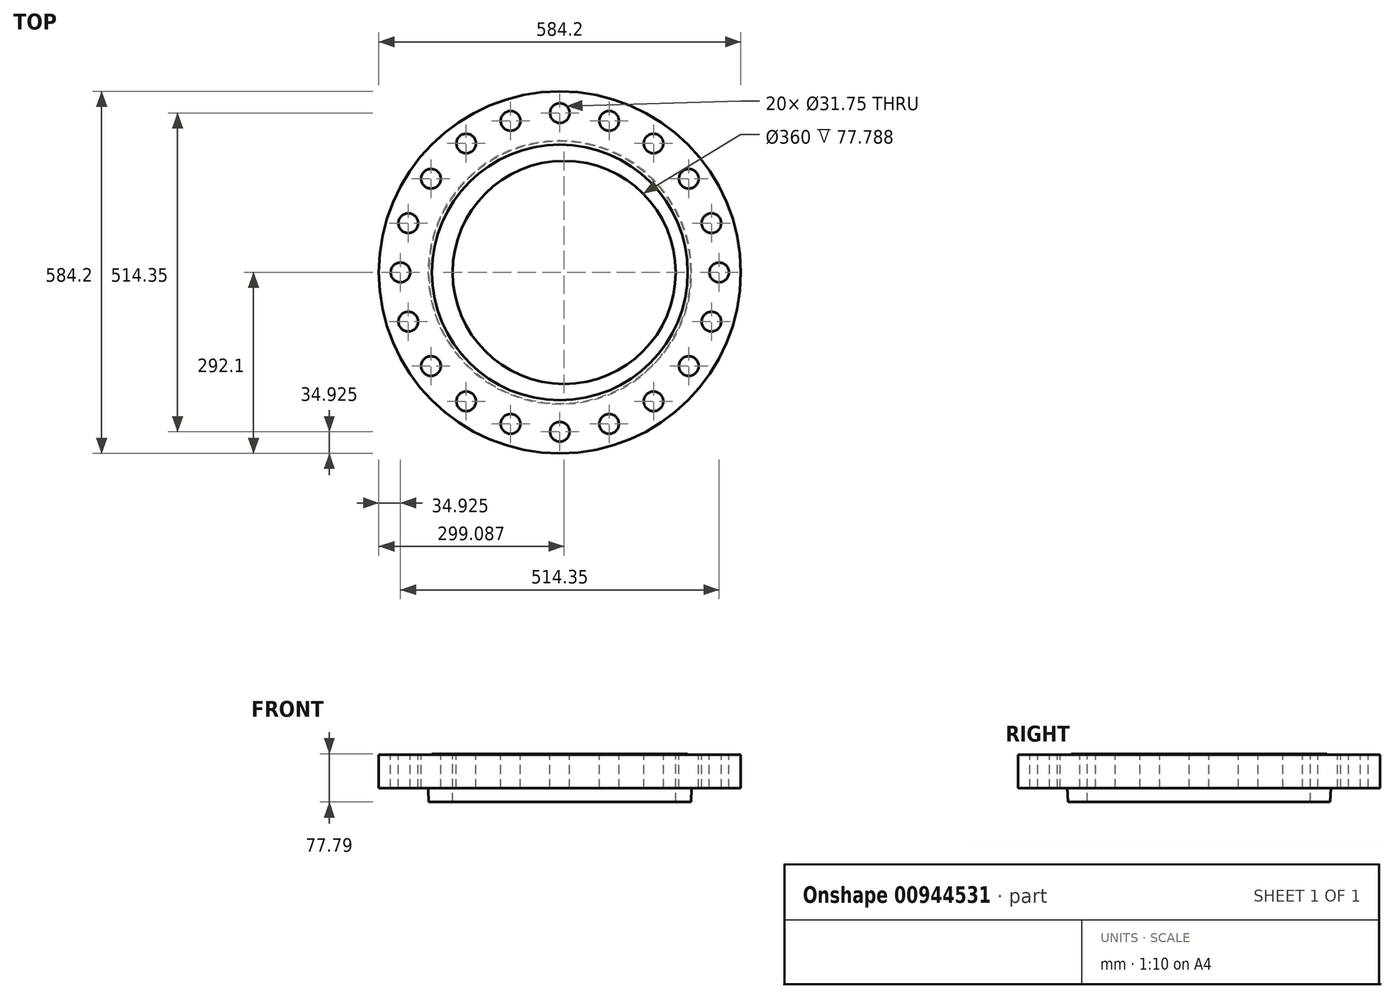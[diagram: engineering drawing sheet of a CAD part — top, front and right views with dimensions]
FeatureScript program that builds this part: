
annotation { "Feature Type Name" : "Feature", "Feature Type Description" : "" }
export const myFeature = defineFeature(function(context is Context, id is Id, definition is map)
    precondition{}
    {
        {
            var Q0;
            Q0=qCreatedBy(makeId("Top.planeOp"),FACE);
            var sketch = newSketch(context, id + "F0", { "sketchPlane" : qUnion([Q0])});
            skCircle(sketch, "E0", {"center": v(0, 0) * mm, "radius": 292.1 * mm});
            skSolve(sketch);
        }
        {
            var Q0;
            Q0=makeQuery(id+"F0.imprint","IMPRINT",FACE,{"disambiguationData":[TD([[makeQuery(id+"F0.imprint","IMPRINT",EDGE,{"derivedFrom":sQuery(id+"F0.wireOp",EDGE,"E0")}),1.0]])]});
            extrude(context, id + "F1", {"entities" : qUnion([Q0]), "oppositeDirection" : true, "depth" : 53.98 * mm, "offsetDistance" : 25 * mm});
        }
        {
            var Q0;
            Q0=makeQuery(id+"F1.opExtrude","CAP_FACE",FACE,{"disambiguationData":[OSD([sQuery(id+"F0.wireOp",EDGE,"E0")])],"isStart":true});
            var sketch = newSketch(context, id + "F2", { "sketchPlane" : qUnion([Q0])});
            skCircle(sketch, "E1", {"center": v(0, 0) * mm, "radius": 206.38 * mm});
            skSolve(sketch);
        }
        {
            var Q0;
            Q0 = qSketchRegion(id + "F2", true);
            extrude(context, id + "F3", {"entities" : qUnion([Q0]), "operationType" : NewBodyOperationType.ADD, "depth" : 1.59 * mm, "offsetDistance" : 25 * mm});
        }
        {
            var Q0;
            Q0=makeQuery(id+"F1.opExtrude","CAP_FACE",FACE,{"disambiguationData":[OSD([sQuery(id+"F0.wireOp",EDGE,"E0")])],"isStart":false});
            var sketch = newSketch(context, id + "F4", { "sketchPlane" : qUnion([Q0])});
            skCircle(sketch, "E2", {"center": v(0, 0) * mm, "radius": 212.72 * mm});
            skSolve(sketch);
        }
        {
            var Q0;
            Q0 = qSketchRegion(id + "F4", true);
            extrude(context, id + "F5", {"entities" : qUnion([Q0]), "operationType" : NewBodyOperationType.ADD, "depth" : 22.23 * mm, "offsetDistance" : 25 * mm, "hasDraft" : true, "draftAngle" : 3 * degree, "draftPullDirection" : true});
        }
        {
            var Q0;
            Q0=makeQuery(id+"F3.opExtrude","CAP_FACE",FACE,{"disambiguationData":[OSD([sQuery(id+"F2.wireOp",EDGE,"E1")])],"isStart":false});
            var sketch = newSketch(context, id + "F6", { "sketchPlane" : qUnion([Q0])});
            skCircle(sketch, "E3", {"center": v(6.99, 0) * mm, "radius": 180 * mm});
            skSolve(sketch);
        }
        {
            var Q0;
            Q0=makeQuery(id+"F6.imprint","IMPRINT",FACE,{"disambiguationData":[TD([[makeQuery(id+"F6.imprint","IMPRINT",EDGE,{"derivedFrom":sQuery(id+"F6.wireOp",EDGE,"E3")}),1.0]])]});
            extrude(context, id + "F7", {"entities" : qUnion([Q0]), "operationType" : NewBodyOperationType.REMOVE, "endBound" : BoundingType.THROUGH_ALL, "oppositeDirection" : true, "depth" : 25 * mm, "offsetDistance" : 25 * mm});
        }
        {
            var Q0;
            Q0=makeQuery(id+"F1.opExtrude","CAP_FACE",FACE,{"disambiguationData":[OSD([sQuery(id+"F0.wireOp",EDGE,"E0")])],"isStart":true});
            var sketch = newSketch(context, id + "F8", { "sketchPlane" : qUnion([Q0])});
            skCircle(sketch, "E4", {"center": v(0, 0) * mm, "radius": 257.18 * mm});
            skCircle(sketch, "E5", {"center": v(257.18, 0) * mm, "radius": 15.88 * mm});
            skCircle(sketch, "E6.1.0", {"center": v(244.59, 79.47) * mm, "radius": 15.88 * mm});
            skCircle(sketch, "E6.2.0", {"center": v(208.06, 151.16) * mm, "radius": 15.88 * mm});
            skCircle(sketch, "E6.3.0", {"center": v(151.16, 208.06) * mm, "radius": 15.88 * mm});
            skCircle(sketch, "E6.4.0", {"center": v(79.47, 244.59) * mm, "radius": 15.88 * mm});
            skCircle(sketch, "E6.5.0", {"center": v(0, 257.18) * mm, "radius": 15.88 * mm});
            skCircle(sketch, "E6.6.0", {"center": v(-79.47, 244.59) * mm, "radius": 15.88 * mm});
            skCircle(sketch, "E6.7.0", {"center": v(-151.16, 208.06) * mm, "radius": 15.87 * mm});
            skCircle(sketch, "E6.8.0", {"center": v(-208.06, 151.16) * mm, "radius": 15.88 * mm});
            skCircle(sketch, "E6.9.0", {"center": v(-244.59, 79.47) * mm, "radius": 15.88 * mm});
            skCircle(sketch, "E6.10.0", {"center": v(-257.18, 0) * mm, "radius": 15.88 * mm});
            skCircle(sketch, "E6.11.0", {"center": v(-244.59, -79.47) * mm, "radius": 15.88 * mm});
            skCircle(sketch, "E6.12.0", {"center": v(-208.06, -151.16) * mm, "radius": 15.88 * mm});
            skCircle(sketch, "E6.13.0", {"center": v(-151.16, -208.06) * mm, "radius": 15.88 * mm});
            skCircle(sketch, "E6.14.0", {"center": v(-79.47, -244.59) * mm, "radius": 15.88 * mm});
            skCircle(sketch, "E6.15.0", {"center": v(0, -257.18) * mm, "radius": 15.88 * mm});
            skCircle(sketch, "E6.16.0", {"center": v(79.47, -244.59) * mm, "radius": 15.88 * mm});
            skCircle(sketch, "E6.17.0", {"center": v(151.16, -208.06) * mm, "radius": 15.88 * mm});
            skCircle(sketch, "E6.18.0", {"center": v(208.06, -151.16) * mm, "radius": 15.88 * mm});
            skCircle(sketch, "E6.19.0", {"center": v(244.59, -79.47) * mm, "radius": 15.88 * mm});
            skSolve(sketch);
        }
        {
            var Q0;
            Q0=sQuery(id+"F8.wireOp",VERTEX,"E6.1.0.center");
            var Q1;
            Q1=sQuery(id+"F8.wireOp",VERTEX,"E6.2.0.center");
            var Q2;
            Q2=sQuery(id+"F8.wireOp",VERTEX,"E6.3.0.center");
            var Q3;
            Q3=sQuery(id+"F8.wireOp",VERTEX,"E6.4.0.center");
            var Q4;
            Q4=sQuery(id+"F8.wireOp",VERTEX,"E6.5.0.center");
            var Q5;
            Q5=sQuery(id+"F8.wireOp",VERTEX,"E6.6.0.center");
            var Q6;
            Q6=sQuery(id+"F8.wireOp",VERTEX,"E6.7.0.center");
            var Q7;
            Q7=sQuery(id+"F8.wireOp",VERTEX,"E6.8.0.center");
            var Q8;
            Q8=sQuery(id+"F8.wireOp",VERTEX,"E6.9.0.center");
            var Q9;
            Q9=sQuery(id+"F8.wireOp",VERTEX,"E6.10.0.center");
            var Q10;
            Q10=sQuery(id+"F8.wireOp",VERTEX,"E6.11.0.center");
            var Q11;
            Q11=sQuery(id+"F8.wireOp",VERTEX,"E6.12.0.center");
            var Q12;
            Q12=sQuery(id+"F8.wireOp",VERTEX,"E6.13.0.center");
            var Q13;
            Q13=sQuery(id+"F8.wireOp",VERTEX,"E6.14.0.center");
            var Q14;
            Q14=sQuery(id+"F8.wireOp",VERTEX,"E6.15.0.center");
            var Q15;
            Q15=sQuery(id+"F8.wireOp",VERTEX,"E6.16.0.center");
            var Q16;
            Q16=sQuery(id+"F8.wireOp",VERTEX,"E6.17.0.center");
            var Q17;
            Q17=sQuery(id+"F8.wireOp",VERTEX,"E6.18.0.center");
            var Q18;
            Q18=sQuery(id+"F8.wireOp",VERTEX,"E6.19.0.center");
            var Q19;
            Q19=sQuery(id+"F8.wireOp",VERTEX,"E5.center");
            var Q20;
            Q20=makeQuery(id+"F1.opExtrude","SWEPT_BODY",BODY,{"disambiguationData":[OSD([sQuery(id+"F0.wireOp",EDGE,"E0")])]});
            hole(context, id + "F9", {"style" : HoleStyle.SIMPLE, "endStyle" : HoleEndStyle.THROUGH, "holeDiameter" : 31.75 * mm, "majorDiameter" : 5 * mm, "isTappedThrough" : true, "tappedDepth" : 12 * mm, "tapClearance" : 3, "locations" : qUnion([Q0, Q1, Q2, Q3, Q4, Q5, Q6, Q7, Q8, Q9, Q10, Q11, Q12, Q13, Q14, Q15, Q16, Q17, Q18, Q19]), "scope" : qUnion([Q20])});
        }
    });
